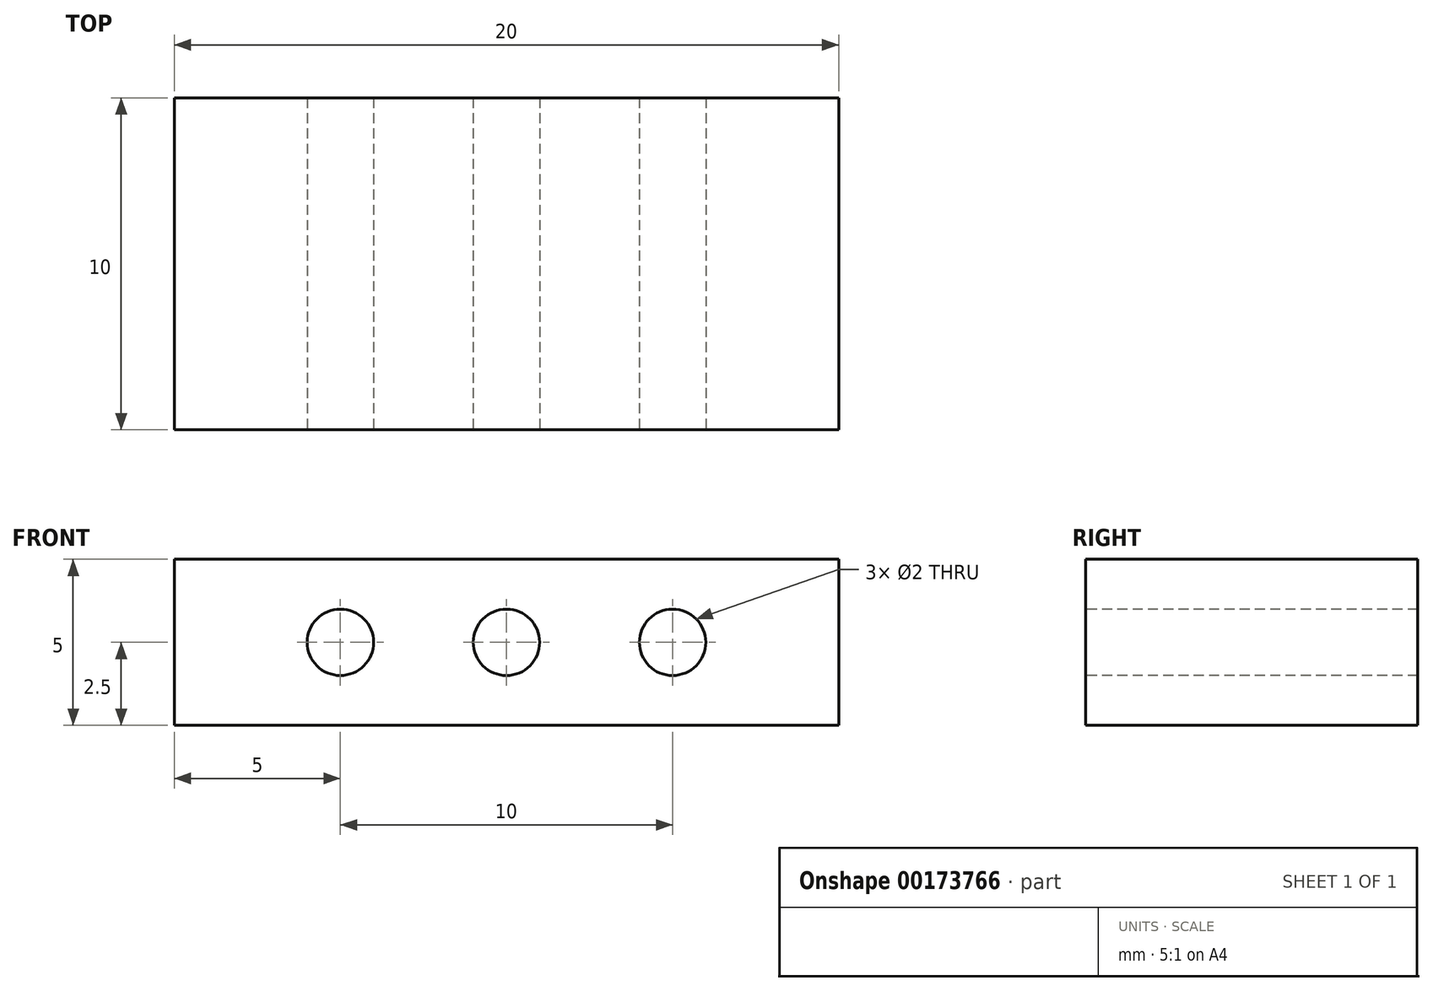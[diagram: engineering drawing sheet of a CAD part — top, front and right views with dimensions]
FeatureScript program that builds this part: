
annotation { "Feature Type Name" : "Feature", "Feature Type Description" : "" }
export const myFeature = defineFeature(function(context is Context, id is Id, definition is map)
    precondition{}
    {
        {
            var Q0;
            Q0=qCreatedBy(makeId("Top.planeOp"),FACE);
            var sketch = newSketch(context, id + "F0", { "sketchPlane" : qUnion([Q0])});
            skLineSegment(sketch, "E0.bottom", {"start": v(10, 5) * mm, "end": v(-10, 5) * mm});
            skLineSegment(sketch, "E0.top", {"start": v(10, -5) * mm, "end": v(-10, -5) * mm});
            skLineSegment(sketch, "E0.left", {"start": v(10, 5) * mm, "end": v(10, -5) * mm});
            skLineSegment(sketch, "E0.right", {"start": v(-10, 5) * mm, "end": v(-10, -5) * mm});
            skPoint(sketch, "E0.middle", {"position": v(0, 0) * mm});
            skSolve(sketch);
        }
        {
            var Q0;
            Q0=makeQuery(id+"F0.imprint","IMPRINT",FACE,{"disambiguationData":[TD([[makeQuery(id+"F0.imprint","IMPRINT",EDGE,{"derivedFrom":sQuery(id+"F0.wireOp",EDGE,"E0.bottom")}),1.0]])]});
            extrude(context, id + "F1", {"entities" : qUnion([Q0]), "depth" : 5 * mm});
        }
        {
            var Q0;
            Q0=makeQuery(id+"F1.opExtrude","SWEPT_FACE",FACE,{"disambiguationData":[OSD([sQuery(id+"F0.wireOp",EDGE,"E0.top")])]});
            var sketch = newSketch(context, id + "F2", { "sketchPlane" : qUnion([Q0])});
            skCircle(sketch, "E1", {"center": v(-5, 2.5) * mm, "radius": 1 * mm});
            skCircle(sketch, "E2", {"center": v(0, 2.5) * mm, "radius": 1 * mm});
            skCircle(sketch, "E3", {"center": v(5, 2.5) * mm, "radius": 1 * mm});
            skSolve(sketch);
        }
        {
            var Q0;
            Q0 = qSketchRegion(id + "F2", true);
            extrude(context, id + "F3", {"entities" : qUnion([Q0]), "operationType" : NewBodyOperationType.REMOVE, "endBound" : BoundingType.UP_TO_NEXT, "oppositeDirection" : true, "depth" : 25 * mm});
        }
    });
